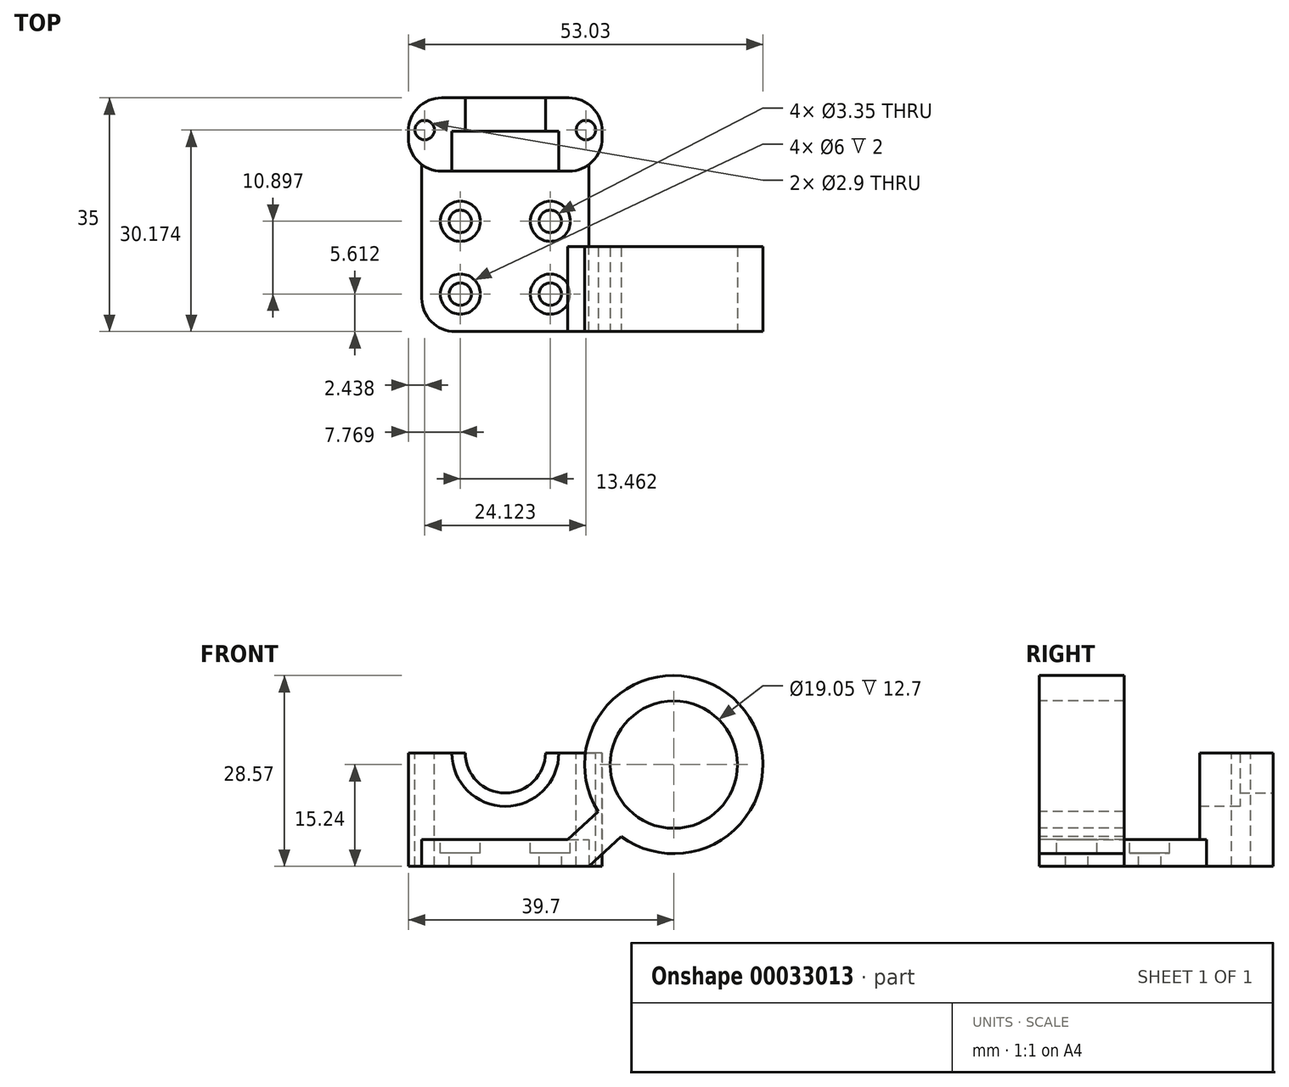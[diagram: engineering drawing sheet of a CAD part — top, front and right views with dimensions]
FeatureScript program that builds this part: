
annotation { "Feature Type Name" : "Feature", "Feature Type Description" : "" }
export const myFeature = defineFeature(function(context is Context, id is Id, definition is map)
    precondition{}
    {
        {
            var Q0;
            Q0=qCreatedBy(makeId("Top.planeOp"),FACE);
            var sketch = newSketch(context, id + "F0", { "sketchPlane" : qUnion([Q0])});
            skLineSegment(sketch, "E0.bottom", {"start": v(0, 0) * mm, "end": v(25, 0) * mm});
            skLineSegment(sketch, "E0.top", {"start": v(0, 35) * mm, "end": v(25, 35) * mm});
            skLineSegment(sketch, "E0.left", {"start": v(0, 0) * mm, "end": v(0, 35) * mm});
            skLineSegment(sketch, "E0.right", {"start": v(25, 0) * mm, "end": v(25, 35) * mm});
            skSolve(sketch);
        }
        {
            var Q0;
            Q0=qSketchRegion(id+"F0",true);
            extrude(context, id + "F1", {"entities" : qUnion([Q0]), "depth" : 4 * mm});
        }
        {
            var Q0;
            Q0=makeQuery(id+"F1.opExtrude","CAP_FACE",FACE,{"disambiguationData":[OSD([sQuery(id+"F0.wireOp",EDGE,"E0.bottom"),sQuery(id+"F0.wireOp",EDGE,"E0.top"),sQuery(id+"F0.wireOp",EDGE,"E0.left"),sQuery(id+"F0.wireOp",EDGE,"E0.right")])],"isStart":false});
            var sketch = newSketch(context, id + "F2", { "sketchPlane" : qUnion([Q0])});
            skCircle(sketch, "E1", {"center": v(5.77, 16.5) * mm, "radius": 1.68 * mm});
            skCircle(sketch, "E2", {"center": v(19.23, 16.5) * mm, "radius": 1.68 * mm});
            skCircle(sketch, "E3", {"center": v(5.77, 5.61) * mm, "radius": 1.68 * mm});
            skCircle(sketch, "E4", {"center": v(19.23, 5.61) * mm, "radius": 1.68 * mm});
            skLineSegment(sketch, "E5", {"start": v(5.77, 16.5) * mm, "end": v(0, 16.5) * mm});
            skLineSegment(sketch, "E6", {"start": v(19.23, 5.61) * mm, "end": v(25, 5.61) * mm});
            skCircle(sketch, "E7", {"center": v(5.77, 16.5) * mm, "radius": 3 * mm});
            skCircle(sketch, "E8", {"center": v(19.23, 16.5) * mm, "radius": 3 * mm});
            skCircle(sketch, "E9", {"center": v(5.77, 5.61) * mm, "radius": 3 * mm});
            skCircle(sketch, "E10", {"center": v(19.23, 5.61) * mm, "radius": 3 * mm});
            skSolve(sketch);
        }
        {
            var Q0;
            Q0=makeQuery(id+"F2.imprint","IMPRINT",FACE,{"disambiguationData":[TD([[makeQuery(id+"F2.imprint","IMPRINT",EDGE,{"derivedFrom":sQuery(id+"F2.wireOp",EDGE,"E1")}),1.0]])]});
            var Q1;
            Q1=makeQuery(id+"F2.imprint","IMPRINT",FACE,{"disambiguationData":[TD([[makeQuery(id+"F2.imprint","IMPRINT",EDGE,{"derivedFrom":sQuery(id+"F2.wireOp",EDGE,"E2")}),1.0]])]});
            var Q2;
            Q2=makeQuery(id+"F2.imprint","IMPRINT",FACE,{"disambiguationData":[TD([[makeQuery(id+"F2.imprint","IMPRINT",EDGE,{"derivedFrom":sQuery(id+"F2.wireOp",EDGE,"E4")}),1.0]])]});
            var Q3;
            Q3=makeQuery(id+"F2.imprint","IMPRINT",FACE,{"disambiguationData":[TD([[makeQuery(id+"F2.imprint","IMPRINT",EDGE,{"derivedFrom":sQuery(id+"F2.wireOp",EDGE,"E3")}),1.0]])]});
            extrude(context, id + "F3", {"entities" : qUnion([Q0, Q1, Q2, Q3]), "operationType" : NewBodyOperationType.REMOVE, "oppositeDirection" : true, "depth" : 25 * mm});
        }
        {
            var Q0;
            Q0=makeQuery(id+"F1.opExtrude","CAP_FACE",FACE,{"disambiguationData":[OSD([sQuery(id+"F0.wireOp",EDGE,"E0.bottom"),sQuery(id+"F0.wireOp",EDGE,"E0.top"),sQuery(id+"F0.wireOp",EDGE,"E0.left"),sQuery(id+"F0.wireOp",EDGE,"E0.right")])],"isStart":false});
            var sketch = newSketch(context, id + "F4", { "sketchPlane" : qUnion([Q0])});
            skLineSegment(sketch, "E11.bottom", {"start": v(0, 35) * mm, "end": v(25, 35) * mm});
            skLineSegment(sketch, "E11.top", {"start": v(0, 24) * mm, "end": v(25, 24) * mm});
            skLineSegment(sketch, "E11.left", {"start": v(0, 35) * mm, "end": v(0, 24) * mm});
            skLineSegment(sketch, "E11.right", {"start": v(25, 35) * mm, "end": v(25, 24) * mm});
            skSolve(sketch);
        }
        {
            var Q0;
            Q0=qSketchRegion(id+"F4",true);
            extrude(context, id + "F5", {"entities" : qUnion([Q0]), "operationType" : NewBodyOperationType.ADD, "depth" : 13 * mm});
        }
        {
            var Q0;
            Q0=makeQuery(id+"F5.boolean.opBoolean","MERGE",FACE,{"derivedFrom":[makeQuery(id+"F1.opExtrude","SWEPT_FACE",FACE,{"disambiguationData":[OSD([sQuery(id+"F0.wireOp",EDGE,"E0.top")])]}),makeQuery(id+"F5.opExtrude","SWEPT_FACE",FACE,{"disambiguationData":[OSD([sQuery(id+"F4.wireOp",EDGE,"E11.bottom")])]})]});
            var sketch = newSketch(context, id + "F6", { "sketchPlane" : qUnion([Q0])});
            skCircle(sketch, "E12", {"center": v(-12.5, 17) * mm, "radius": 6 * mm});
            skSolve(sketch);
        }
        {
            var Q0;
            {var subQ0=makeQuery(id+"F5.opExtrude","CAP_EDGE",EDGE,{"disambiguationData":[OSD([sQuery(id+"F4.wireOp",EDGE,"E11.bottom")])],"isStart":false});var subQ1=sQuery(id+"F6.wireOp",EDGE,"E12");var subQ3=makeQuery(id+"F6.imprint","INTERSECT",VERTEX,{"disambiguationData":[OD(0.0)],"derivedFrom":[subQ0,subQ1]});Q0=makeQuery(id+"F6.imprint","IMPRINT",FACE,{"disambiguationData":[TD([[makeQuery(id+"F6.imprint","IMPRINT",EDGE,{"disambiguationData":[TD([[subQ3,1.0]])],"derivedFrom":subQ1}),1.0]])]});}
            extrude(context, id + "F7", {"entities" : qUnion([Q0]), "operationType" : NewBodyOperationType.REMOVE, "oppositeDirection" : true, "depth" : 6 * mm});
        }
        {
            var Q0;
            Q0=makeQuery(id+"F5.opExtrude","SWEPT_FACE",FACE,{"disambiguationData":[OSD([sQuery(id+"F4.wireOp",EDGE,"E11.top")])]});
            var sketch = newSketch(context, id + "F8", { "sketchPlane" : qUnion([Q0])});
            skCircle(sketch, "E13", {"center": v(12.5, 17) * mm, "radius": 8 * mm});
            skSolve(sketch);
        }
        {
            var Q0;
            Q0=qSketchRegion(id+"F8",true);
            extrude(context, id + "F9", {"entities" : qUnion([Q0]), "operationType" : NewBodyOperationType.REMOVE, "oppositeDirection" : true, "depth" : 6 * mm});
        }
        {
            var Q0;
            Q0=makeQuery(id+"F2.imprint","IMPRINT",FACE,{"disambiguationData":[TD([[makeQuery(id+"F2.imprint","IMPRINT",EDGE,{"derivedFrom":sQuery(id+"F2.wireOp",EDGE,"E1")}),-1.0]])]});
            var Q1;
            Q1=makeQuery(id+"F2.imprint","IMPRINT",FACE,{"disambiguationData":[TD([[makeQuery(id+"F2.imprint","IMPRINT",EDGE,{"derivedFrom":sQuery(id+"F2.wireOp",EDGE,"E2")}),-1.0]])]});
            var Q2;
            Q2=makeQuery(id+"F2.imprint","IMPRINT",FACE,{"disambiguationData":[TD([[makeQuery(id+"F2.imprint","IMPRINT",EDGE,{"derivedFrom":sQuery(id+"F2.wireOp",EDGE,"E4")}),-1.0]])]});
            var Q3;
            Q3=makeQuery(id+"F2.imprint","IMPRINT",FACE,{"disambiguationData":[TD([[makeQuery(id+"F2.imprint","IMPRINT",EDGE,{"derivedFrom":sQuery(id+"F2.wireOp",EDGE,"E3")}),-1.0]])]});
            extrude(context, id + "F10", {"entities" : qUnion([Q0, Q1, Q2, Q3]), "operationType" : NewBodyOperationType.REMOVE, "oppositeDirection" : true, "depth" : 2 * mm});
        }
        {
            var Q0;
            Q0=makeQuery(id+"F5.boolean.opBoolean","MERGE",FACE,{"derivedFrom":[makeQuery(id+"F1.opExtrude","SWEPT_FACE",FACE,{"disambiguationData":[OSD([sQuery(id+"F0.wireOp",EDGE,"E0.left")])]}),makeQuery(id+"F5.opExtrude","SWEPT_FACE",FACE,{"disambiguationData":[OSD([sQuery(id+"F4.wireOp",EDGE,"E11.left")])]})]});
            var sketch = newSketch(context, id + "F11", { "sketchPlane" : qUnion([Q0])});
            skLineSegment(sketch, "E14.bottom", {"start": v(-35, 0) * mm, "end": v(-24, 0) * mm});
            skLineSegment(sketch, "E14.top", {"start": v(-35, 17) * mm, "end": v(-24, 17) * mm});
            skLineSegment(sketch, "E14.left", {"start": v(-35, 0) * mm, "end": v(-35, 17) * mm});
            skLineSegment(sketch, "E14.right", {"start": v(-24, 0) * mm, "end": v(-24, 17) * mm});
            skSolve(sketch);
        }
        {
            var Q0;
            Q0=qSketchRegion(id+"F11",true);
            extrude(context, id + "F12", {"entities" : qUnion([Q0]), "operationType" : NewBodyOperationType.ADD, "depth" : 2 * mm});
        }
        {
            var Q0;
            Q0=makeQuery(id+"F5.boolean.opBoolean","MERGE",FACE,{"derivedFrom":[makeQuery(id+"F1.opExtrude","SWEPT_FACE",FACE,{"disambiguationData":[OSD([sQuery(id+"F0.wireOp",EDGE,"E0.right")])]}),makeQuery(id+"F5.opExtrude","SWEPT_FACE",FACE,{"disambiguationData":[OSD([sQuery(id+"F4.wireOp",EDGE,"E11.right")])]})]});
            var sketch = newSketch(context, id + "F13", { "sketchPlane" : qUnion([Q0])});
            skLineSegment(sketch, "E15.bottom", {"start": v(35, 0) * mm, "end": v(24, 0) * mm});
            skLineSegment(sketch, "E15.top", {"start": v(35, 17) * mm, "end": v(24, 17) * mm});
            skLineSegment(sketch, "E15.left", {"start": v(35, 0) * mm, "end": v(35, 17) * mm});
            skLineSegment(sketch, "E15.right", {"start": v(24, 0) * mm, "end": v(24, 17) * mm});
            skSolve(sketch);
        }
        {
            var Q0;
            Q0=qSketchRegion(id+"F13",true);
            extrude(context, id + "F14", {"entities" : qUnion([Q0]), "operationType" : NewBodyOperationType.ADD, "depth" : 2 * mm});
        }
        {
            var Q0;
            {var subQ0=sQuery(id+"F4.wireOp",EDGE,"E11.bottom");var subQ1=sQuery(id+"F4.wireOp",EDGE,"E11.top");var subQ2=sQuery(id+"F4.wireOp",EDGE,"E11.left");Q0=makeQuery(id+"F9.boolean.opBoolean","SPLIT",FACE,{"disambiguationData":[TD([makeQuery(id+"F1.opExtrude","SWEPT_FACE",FACE,{"disambiguationData":[OSD([sQuery(id+"F0.wireOp",EDGE,"E0.left")])]})])],"derivedFrom":makeQuery(id+"F5.opExtrude","CAP_FACE",FACE,{"disambiguationData":[OSD([subQ0,subQ1,subQ2,sQuery(id+"F4.wireOp",EDGE,"E11.right")])],"isStart":false})});}
            var sketch = newSketch(context, id + "F15", { "sketchPlane" : qUnion([Q0])});
            skCircle(sketch, "E16", {"center": v(0.44, 30.17) * mm, "radius": 1.45 * mm});
            skCircle(sketch, "E17", {"center": v(24.56, 30.17) * mm, "radius": 1.45 * mm});
            skSolve(sketch);
        }
        {
            var Q0;
            Q0=qSketchRegion(id+"F15",true);
            extrude(context, id + "F16", {"entities" : qUnion([Q0]), "operationType" : NewBodyOperationType.REMOVE, "oppositeDirection" : true, "depth" : 25 * mm});
        }
        {
            var Q0;
            Q0=makeQuery(id+"F12.opExtrude","CAP_EDGE",EDGE,{"disambiguationData":[OSD([sQuery(id+"F11.wireOp",EDGE,"E14.right")])],"isStart":false});
            var Q1;
            Q1=makeQuery(id+"F12.opExtrude","CAP_EDGE",EDGE,{"disambiguationData":[OSD([sQuery(id+"F11.wireOp",EDGE,"E14.left")])],"isStart":false});
            var Q2;
            Q2=makeQuery(id+"F14.opExtrude","CAP_EDGE",EDGE,{"disambiguationData":[OSD([sQuery(id+"F13.wireOp",EDGE,"E15.left")])],"isStart":false});
            var Q3;
            Q3=makeQuery(id+"F14.opExtrude","CAP_EDGE",EDGE,{"disambiguationData":[OSD([sQuery(id+"F13.wireOp",EDGE,"E15.right")])],"isStart":false});
            fillet(context, id + "F17", {"entities" : qUnion([Q0, Q1, Q2, Q3]), "radius" : 5 * mm, "tangentPropagation" : true, "allowEdgeOverflow" : false});
        }
        {
            var Q0;
            Q0=makeQuery(id+"F1.opExtrude","SWEPT_FACE",FACE,{"disambiguationData":[OSD([sQuery(id+"F0.wireOp",EDGE,"E0.bottom")])]});
            var sketch = newSketch(context, id + "F18", { "sketchPlane" : qUnion([Q0])});
            skLineSegment(sketch, "E18", {"start": v(25, 0) * mm, "end": v(29.83, 4.48) * mm});
            skLineSegment(sketch, "E19", {"start": v(29.83, 4.48) * mm, "end": v(26.37, 8.2) * mm});
            skLineSegment(sketch, "E20", {"start": v(26.37, 8.2) * mm, "end": v(21.84, 4) * mm});
            skCircle(sketch, "E21", {"center": v(37.7, 15.24) * mm, "radius": 9.53 * mm});
            skCircle(sketch, "E22", {"center": v(37.7, 15.24) * mm, "radius": 13.33 * mm});
            skLineSegment(sketch, "E23", {"start": v(21.84, 4) * mm, "end": v(25, 0) * mm});
            skLineSegment(sketch, "E24", {"start": v(0, 0) * mm, "end": v(70.67, 0) * mm, "construction": true});
            skSolve(sketch);
        }
        {
            var Q0;
            {var subQ0=sQuery(id+"F18.wireOp",EDGE,"E19");Q0=makeQuery(id+"F18.imprint","IMPRINT",FACE,{"disambiguationData":[TD([[makeQuery(id+"F18.imprint","IMPRINT",EDGE,{"derivedFrom":subQ0}),-1.0]])]});}
            var Q1;
            {var subQ4=sQuery(id+"F18.wireOp",EDGE,"E18");Q1=makeQuery(id+"F18.imprint","IMPRINT",FACE,{"disambiguationData":[TD([[makeQuery(id+"F18.imprint","IMPRINT",EDGE,{"derivedFrom":subQ4}),1.0]])]});}
            var Q2;
            {var subQ0=sQuery(id+"F18.wireOp",EDGE,"E19");Q2=makeQuery(id+"F18.imprint","IMPRINT",FACE,{"disambiguationData":[TD([[makeQuery(id+"F18.imprint","IMPRINT",EDGE,{"derivedFrom":subQ0}),1.0]])]});}
            extrude(context, id + "F19", {"entities" : qUnion([Q0, Q1, Q2]), "operationType" : NewBodyOperationType.ADD, "oppositeDirection" : true, "depth" : 12.7 * mm, "offsetDistance" : 25.4 * mm});
        }
        {
            var Q0;
            Q0=makeQuery(id+"F1.opExtrude","SWEPT_EDGE",EDGE,{"disambiguationData":[OSD([sQuery(id+"F0.wireOp",EDGE,"E0.bottom"),sQuery(id+"F0.wireOp",EDGE,"E0.left")])]});
            var Q1;
            Q1=makeQuery(id+"F1.opExtrude","SWEPT_EDGE",EDGE,{"disambiguationData":[OSD([sQuery(id+"F0.wireOp",EDGE,"E0.bottom"),sQuery(id+"F0.wireOp",EDGE,"E0.right")])]});
            fillet(context, id + "F20", {"entities" : qUnion([Q0, Q1]), "radius" : 5 * mm, "tangentPropagation" : true, "allowEdgeOverflow" : false});
        }
    });
